# Revit family: Flush_Valve-Urinal_Concealed-American_Standard-Selectronic-Exposed_Back_Spud-606B5XX_Series
name_source: partatom
category: Plumbing Fixtures
units: mm (PartAtom-declared; Revit-internal decimal feet)

## family parameters
Cut with Voids When Loaded = Yes
Host = Face
OmniClass Number = 23.65.70.00
OmniClass Title = Terminals for Supplied Liquids and Gases
Part Type = Normal
Room Calculation Point = No
Round Connector Dimension = Use Diameter
Shared = Yes

## types (3) — shared parameters
ADA Compliant = Yes
Assembly Code = D2020100
CW Connection = Yes
CWFU = 5
Cold Water Connection Diameter = 3/4"
Cold Water Connection Radius = 3/8"
Critical Line Distance from Tube = 6"
Default Elevation = 0"
Description = Ultima Selectronic Sensor Operated Concealed Urinal Flush Valve
Finish = Brass-American Standard-Satin Brass
Finish - Wall Box = Stainless Steel-American Standard-007-Chrome
HW Connection = No
Height = 11"
Installation Type = Concealed, Back Spud
Manufacturer = American Standard
Material = Brass-American Standard-Satin Brass
NPT Distance to Valve = 5 1/4"
Operating Pressure = 20 psi (flowing) - 80 psi (static)
PK00.CRP Power Kit = No
PK00.HAC Power Kit = No
PK00.MAC Power Kit = No
PK00.PAC Power Kit = No
PK00.WRK Power Kit = No
Price = Prices may vary. Please consult Manufacturer Representative for most up-to-date price list.
Product Documentation Link = https://americanstandard.box.com
Revised Date = 10/01/2021
Tube Length to Wall = 5"
Tube Length to Wall Constraint = 5"
Type Comments = Power Kits Must Be Purchased Separately.
URL = http://www.americanstandard-us.com
Vent Connection = No
WFU = 5
Warranty Information = 1 Year Limited Warranty
Waste Connection = No
Width = 15 7/8"
zero-valued in all types: HWFU

## per-type parameters (varying)
| type | Critical Line Distance from Tube Constraint | Flush Rate | NPT Distance to Valve Constraint | Product Page URL |
| 606B.501.007 | 6" | 0.125 gpf/0.5 Lpf | 5 1/4" | hhttps://www.americanstandard-us.com |
| 606B.510.007 | 5" | 1.0 gpf/0.5 Lpf | 6" | https://www.americanstandard-us.com |
| 606B.505.007 | 6" | 0.5 gpf/1.9 Lpf | 5 1/4" | https://www.americanstandard-us.com |

note: column(s) folded — value = type name in every type: Model

## geometry (parser evidence)
native form markers: Sweep x2
no freeform markers — native parametric forms only
